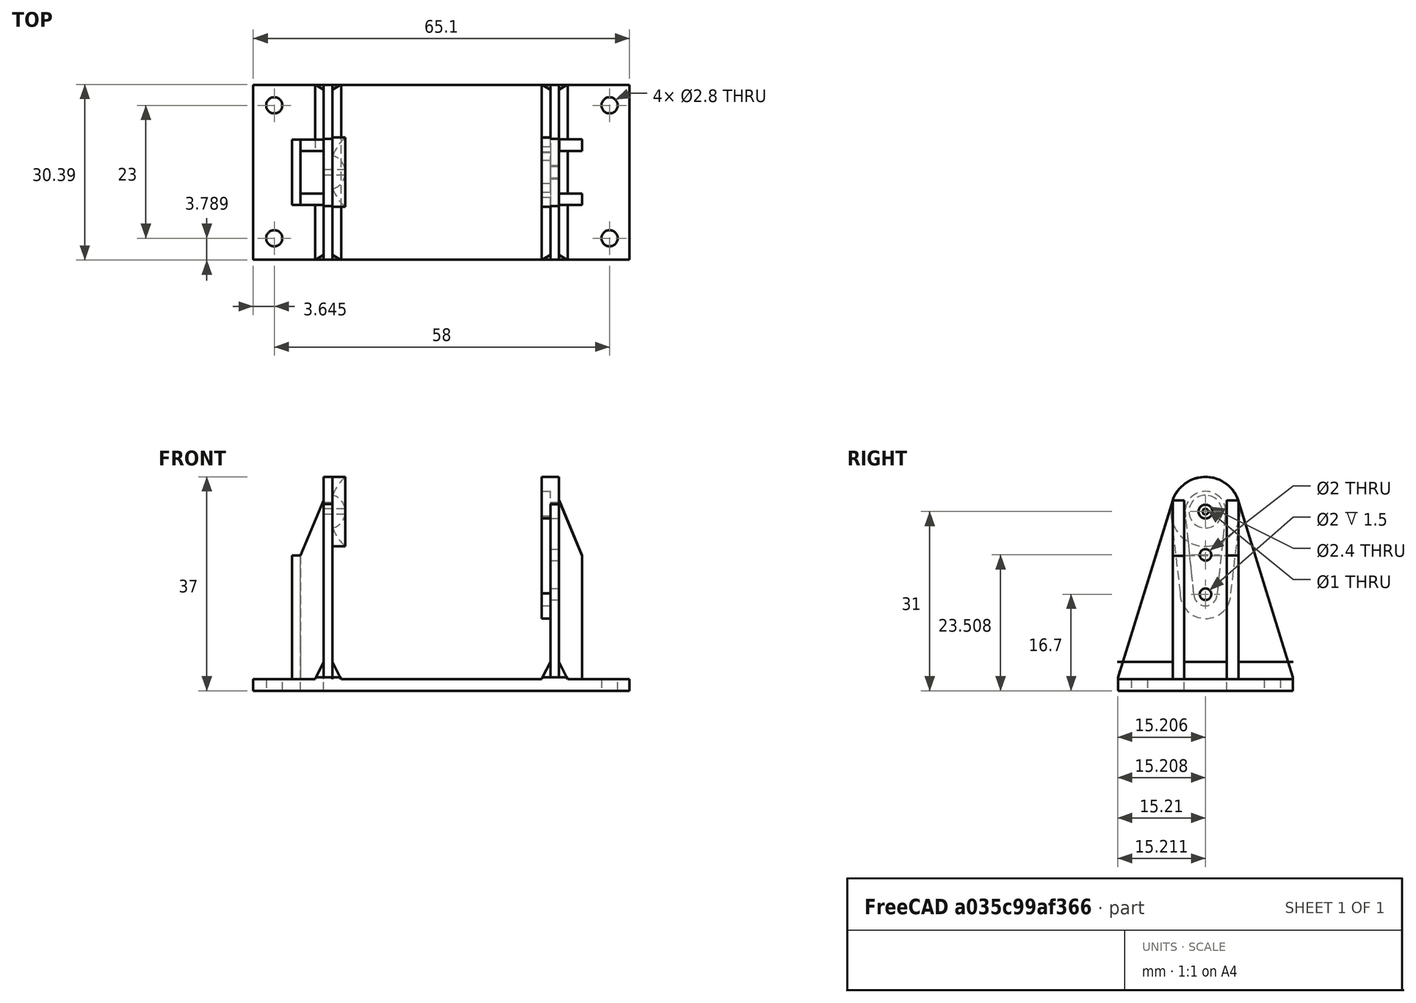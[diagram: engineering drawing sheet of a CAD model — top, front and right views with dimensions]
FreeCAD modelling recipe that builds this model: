
FCSTD DOCUMENT  (FreeCAD 0.18.3R)
Label: Arms
License: All rights reserved
LicenseURL: http://en.wikipedia.org/wiki/All_rights_reserved
objects: Part::Part2DObjectPython×24, Part::Extrusion×17, Part::Cut×11, Part::MultiFuse×6, App::DocumentObjectGroup×2
note: 58 computed .brp shape members not serialized (recipe doc carries the construction recipe); baked Part::Feature solids carry a one-line shape summary decoded from their .brp

FEATURE [Part::Part2DObjectPython] Line006  # Draft 2D object (typed FeaturePython)
  ChamferSize = 0
  Closed = false
  End = (53.5252,-151.594,31)
  FilletRadius = 0
  Length = 2.4
  MakeFace = true
  Placement = pos=(53.5252,-149.194,31) rot=(-1,0,0;1.5708rad)
  Points = (2) [(0,0,0),(0,0,-2.4)]
  Start = (53.5252,-149.194,31)
  Subdivisions = 0
FEATURE [App::DocumentObjectGroup] GrExplode_Slice001  label="Exploded Slice001"
FEATURE [App::DocumentObjectGroup] GrExplode_Slice  label="Exploded Slice"
FEATURE [Part::Part2DObjectPython] Line013  # Draft 2D object (typed FeaturePython)
  ChamferSize = 0
  Closed = false
  End = (34.5802,-150.49,31)
  FilletRadius = 0
  Length = 29
  MakeFace = true
  Placement = pos=(34.5802,-150.506,2) rot=(0.57735,-0.57735,0.57735;4.18879rad)
  Points = (2) [(0,0,0),(-0.0156504,-29,-7.19697e-07)]
  Start = (34.5802,-150.506,2)
  Subdivisions = 0
FEATURE [Part::Part2DObjectPython] Line010  # Draft 2D object (typed FeaturePython)
  ChamferSize = 0
  Closed = false
  End = (15.7302,-144.391,31)
  FilletRadius = 0
  Length = 12.2
  MakeFace = true
  Placement = pos=(15.7302,-156.591,31) rot=(0.57735,-0.57735,0.57735;4.18879rad)
  Points = (2) [(0,0,0),(-12.2,0,0)]
  Start = (15.7302,-156.591,31)
  Subdivisions = 0
FEATURE [Part::Part2DObjectPython] Line  # Draft 2D object (typed FeaturePython)
  ChamferSize = 0
  Closed = false
  End = (53.4302,-150.489,31)
  FilletRadius = 0
  Length = 37.7
  MakeFace = true
  Placement = pos=(15.7302,-150.491,31) rot=(0.57735,0.57735,-0.57735;4.18879rad)
  Points = (2) [(0,0,0),(0.00173367,0,-37.7)]
  Start = (15.7302,-150.491,31)
  Subdivisions = 0
FEATURE [Part::Part2DObjectPython] Line014  # Draft 2D object (typed FeaturePython)
  ChamferSize = 0
  Closed = false
  End = (67.1302,-150.506,-7.22776)
  FilletRadius = 0
  Length = 16.9555
  MakeFace = true
  Placement = pos=(67.1302,-150.506,9.72776) rot=(0.57735,-0.57735,0.57735;4.18879rad)
  Points = (2) [(0,0,0),(0,16.9555,0)]
  Start = (67.1302,-150.506,9.72776)
  Subdivisions = 0
FEATURE [Part::Part2DObjectPython] Rectangle001  # Draft 2D object (typed FeaturePython)
  ChamferSize = 0
  Columns = 1
  FilletRadius = 0
  Height = 30.9198
  Length = 2
  MakeFace = true
  Placement = pos=(55.0252,-156.055,2) rot=(0.57735,0.57735,0.57735;2.0944rad)
  Rows = 1
FEATURE [Part::Part2DObjectPython] Rectangle002  # Draft 2D object (typed FeaturePython)
  ChamferSize = 0
  Columns = 1
  FilletRadius = 0
  Height = 30.9198
  Length = 2
  MakeFace = true
  Placement = pos=(55.0252,-146.712,2) rot=(0.57735,0.57735,0.57735;2.0944rad)
  Rows = 1
FEATURE [Part::Part2DObjectPython] Rectangle003  # Draft 2D object (typed FeaturePython)
  ChamferSize = 0
  Columns = 1
  FilletRadius = 0
  Height = 30.9198
  Length = 2
  MakeFace = true
  Placement = pos=(14.3252,-156.057,2) rot=(0.57735,0.57735,0.57735;2.0944rad)
  Rows = 1
FEATURE [Part::Part2DObjectPython] Rectangle004  # Draft 2D object (typed FeaturePython)
  ChamferSize = 0
  Columns = 1
  FilletRadius = 0
  Height = 30.9198
  Length = 2
  MakeFace = true
  Placement = pos=(14.3252,-146.735,2.06032) rot=(0.57735,0.57735,0.57735;2.0944rad)
  Rows = 1
FEATURE [Part::Extrusion] Extrude
  Base = -> Rectangle003
  Dir = (1,0,0)
  DirMode = 2
  FaceMakerClass = Part::FaceMakerBullseye
  LengthFwd = -4
  LengthRev = 0
  Solid = false
  Symmetric = false
FEATURE [Part::Extrusion] Extrude001
  Base = -> Rectangle004
  Dir = (1,0,0)
  DirMode = 2
  FaceMakerClass = Part::FaceMakerBullseye
  LengthFwd = -4
  LengthRev = 0
  Solid = false
  Symmetric = false
FEATURE [Part::Extrusion] Extrude002
  Base = -> Rectangle001
  Dir = (1,0,0)
  DirMode = 2
  FaceMakerClass = Part::FaceMakerBullseye
  LengthFwd = 4
  LengthRev = 0
  Solid = false
  Symmetric = false
FEATURE [Part::Extrusion] Extrude003
  Base = -> Rectangle002
  Dir = (1,0,0)
  DirMode = 2
  FaceMakerClass = Part::FaceMakerBullseye
  LengthFwd = 4
  LengthRev = 0
  Solid = false
  Symmetric = false
FEATURE [Part::Part2DObjectPython] Wire  # Draft 2D object (typed FeaturePython)
  ChamferSize = 0
  Closed = true
  End = (59.0252,-156.055,32.9198)
  FilletRadius = 0
  Length = 23.9468
  MakeFace = true
  Placement = pos=(55.0252,-156.055,32.9198) rot=(0.57735,-0.57735,-0.57735;2.0944rad)
  Points = (3) [(0,0,0),(-9.03045e-07,-9.57236,-4),(0,0,-4)]
  Start = (55.0252,-156.055,32.9198)
  Subdivisions = 0
FEATURE [Part::MultiFuse] Fusion053
  Placement = pos=(1.1,-300.821,2.5) rot=(1,0,0;3.14159rad)
FEATURE [Part::Extrusion] Extrude005
  Base = -> Wire
  Dir = (0,11.3221,0.0603199)
  DirLink = -> Fusion053 [Edge102]
  DirMode = 1
  FaceMakerClass = Part::FaceMakerBullseye
  LengthFwd = -29
  LengthRev = -19
  Solid = false
  Symmetric = false
FEATURE [Part::MultiFuse] Fusion
  Shapes = -> [Extrude002,Extrude003]
FEATURE [Part::Cut] Cut
  Base = -> Fusion
  Tool = -> Extrude005
FEATURE [Part::Part2DObjectPython] Circle044  # Draft 2D object (typed FeaturePython)
  FirstAngle = 0
  LastAngle = 0
  MakeFace = true
  Placement = pos=(63.6752,-161.911,0.5) rot=(0,0,1;0rad)
  Radius = 1.4
FEATURE [Part::Extrusion] Extrude179
  Base = -> Circle044
  Dir = (0,0,1)
  DirMode = 2
  FaceMakerClass = Part::FaceMakerBullseye
  LengthFwd = 2
  LengthRev = 0
  Placement = pos=(0,0,-0.5) rot=(0,0,1;0rad)
  Solid = false
  Symmetric = false
FEATURE [Part::Part2DObjectPython] Circle043  # Draft 2D object (typed FeaturePython)
  FirstAngle = 0
  LastAngle = 0
  MakeFace = true
  Placement = pos=(63.6752,-138.911,0.5) rot=(0,0,1;0rad)
  Radius = 1.4
FEATURE [Part::Extrusion] Extrude178
  Base = -> Circle043
  Dir = (0,0,1)
  DirMode = 2
  FaceMakerClass = Part::FaceMakerBullseye
  LengthFwd = 2
  LengthRev = 0
  Placement = pos=(0,0,-0.5) rot=(0,0,1;0rad)
  Solid = false
  Symmetric = false
FEATURE [Part::Part2DObjectPython] Circle041  # Draft 2D object (typed FeaturePython)
  FirstAngle = 0
  LastAngle = 0
  MakeFace = true
  Placement = pos=(5.67515,-138.911,0.5) rot=(0,0,1;0rad)
  Radius = 1.4
FEATURE [Part::Extrusion] Extrude176
  Base = -> Circle041
  Dir = (0,0,1)
  DirMode = 2
  FaceMakerClass = Part::FaceMakerBullseye
  LengthFwd = 2
  LengthRev = 0
  Placement = pos=(0,0,-0.5) rot=(0,0,1;0rad)
  Solid = false
  Symmetric = false
FEATURE [Part::Part2DObjectPython] Circle042  # Draft 2D object (typed FeaturePython)
  FirstAngle = 0
  LastAngle = 0
  MakeFace = true
  Placement = pos=(5.67515,-161.911,0.5) rot=(0,0,1;0rad)
  Radius = 1.4
FEATURE [Part::Extrusion] Extrude177
  Base = -> Circle042
  Dir = (0,0,1)
  DirMode = 2
  FaceMakerClass = Part::FaceMakerBullseye
  LengthFwd = 2
  LengthRev = 0
  Placement = pos=(0,0,-0.5) rot=(0,0,1;0rad)
  Solid = false
  Symmetric = false
FEATURE [Part::Part2DObjectPython] Rectangle073  # Draft 2D object (typed FeaturePython)
  ChamferSize = 0
  Columns = 1
  FilletRadius = 0
  Height = 30.2
  Length = 65.1
  MakeFace = true
  Placement = pos=(2.03015,-165.606,0.5) rot=(0,0,1;0rad)
  Rows = 1
FEATURE [Part::Extrusion] Extrude180
  Base = -> Rectangle073
  Dir = (0,0,1)
  DirMode = 2
  FaceMakerClass = Part::FaceMakerBullseye
  LengthFwd = 2
  LengthRev = 0
  Placement = pos=(0,0,-0.5) rot=(0,0,1;0rad)
  Solid = false
  Symmetric = false
FEATURE [Part::Part2DObjectPython] Rectangle  # Draft 2D object (typed FeaturePython)
  ChamferSize = 0
  Columns = 1
  FilletRadius = 0
  Height = 65.1
  Length = 9.62449
  MakeFace = true
  Placement = pos=(2.03015,-135.406,0.5) rot=(0.707107,0.707107,0;3.14159rad)
  Rows = 1
FEATURE [Part::Extrusion] Extrude181
  Base = -> Rectangle
  Dir = (0,0,-1)
  DirMode = 2
  FaceMakerClass = Part::FaceMakerBullseye
  LengthFwd = -4
  LengthRev = 0
  Solid = false
  Symmetric = false
FEATURE [Part::Part2DObjectPython] Rectangle074  # Draft 2D object (typed FeaturePython)
  ChamferSize = 0
  Columns = 1
  FilletRadius = 0
  Height = 65.1
  Length = 7.3643
  MakeFace = true
  Placement = pos=(2.03015,-172.97,0.5) rot=(0.707107,0.707107,0;3.14159rad)
  Rows = 1
FEATURE [Part::Extrusion] Extrude182
  Base = -> Rectangle074
  Dir = (0,0,-1)
  DirMode = 2
  FaceMakerClass = Part::FaceMakerBullseye
  LengthFwd = -4
  LengthRev = 0
  Solid = false
  Symmetric = false
FEATURE [Part::Cut] Cut100
  Base = -> Extrude180
  Tool = -> Extrude176
FEATURE [Part::Cut] Cut101
  Base = -> Cut100
  Tool = -> Extrude177
FEATURE [Part::Cut] Cut102
  Base = -> Cut101
  Tool = -> Extrude178
FEATURE [Part::Cut] Cut103
  Base = -> Cut102
  Tool = -> Extrude179
FEATURE [Part::Part2DObjectPython] Wire001  # Draft 2D object (typed FeaturePython)
  ChamferSize = 0
  Closed = true
  End = (10.3252,-144.735,32.9801)
  FilletRadius = 0
  Length = 23.9688
  MakeFace = true
  Placement = pos=(14.3252,-144.735,32.9801) rot=(-1,0,0;1.5708rad)
  Points = (3) [(0,0,0),(-4,9.58377,-4.92588e-06),(-4,0,0)]
  Start = (14.3252,-144.735,32.9801)
  Subdivisions = 0
FEATURE [Part::Extrusion] Extrude006
  Base = -> Wire001
  Dir = (0,1,2e-16)
  DirMode = 2
  FaceMakerClass = Part::FaceMakerBullseye
  LengthFwd = -30
  LengthRev = 0
  Solid = false
  Symmetric = false
FEATURE [Part::MultiFuse] Fusion054
  Shapes = -> [Extrude001,Extrude]
FEATURE [Part::Cut] Cut096
  Base = -> Fusion054
  Tool = -> Extrude006
FEATURE [Part::Part2DObjectPython] Wire002  # Draft 2D object (typed FeaturePython)
  ChamferSize = 0
  Closed = true
  End = (10.3252,-144.735,32.9801)
  FilletRadius = 0
  Length = 23.9688
  MakeFace = true
  Placement = pos=(14.3252,-144.735,32.9801) rot=(-1,0,0;1.5708rad)
  Points = (3) [(0,0,0),(-4,9.58377,-4.92588e-06),(-4,0,0)]
  Start = (14.3252,-144.735,32.9801)
  Subdivisions = 0
  Support = -> [Cut096]
FEATURE [Part::Extrusion] Extrude007
  Base = -> Wire002
  Dir = (0,1,2e-16)
  DirMode = 2
  FaceMakerClass = Part::FaceMakerBullseye
  LengthFwd = 10
  LengthRev = 0
  Solid = false
  Symmetric = false
FEATURE [Part::Cut] Cut097
  Base = -> Cut096
  Tool = -> Extrude007
FEATURE [Part::MultiFuse] Fusion055
  Placement = pos=(-0.095,-0.095,-4.9e-15) rot=(0,0,1;0rad)
  Shapes = -> [Fusion053,Cut097,Cut]
FEATURE [Part::Cut] Cut098
  Base = -> Fusion055
  Tool = -> Extrude181
FEATURE [Part::Cut] Cut099
  Base = -> Cut098
  Tool = -> Extrude182
FEATURE [Part::Part2DObjectPython] Rectangle076  # Draft 2D object (typed FeaturePython)
  ChamferSize = 0
  Columns = 1
  FilletRadius = 0
  Height = 21.3963
  Length = 11.3283
  MakeFace = true
  Placement = pos=(10.2302,-144.824,2) rot=(0.57735,-0.57735,-0.57735;2.0944rad)
  Rows = 1
  Support = -> [Cut099]
FEATURE [Part::Extrusion] Extrude184
  Base = -> Rectangle076
  Dir = (-1,0,0)
  DirMode = 2
  FaceMakerClass = Part::FaceMakerBullseye
  LengthFwd = 1.5
  LengthRev = 0
  Solid = false
  Symmetric = false
FEATURE [Part::Part2DObjectPython] Line015  # Draft 2D object (typed FeaturePython)
  ChamferSize = 0
  Closed = false
  End = (14.0481,-156.152,23.3963)
  FilletRadius = 0
  Length = 3.81795
  MakeFace = true
  Placement = pos=(10.2302,-156.152,23.3963) rot=(1,0,0;1.5708rad)
  Points = (2) [(0,0,0),(3.81795,0,0)]
  Start = (10.2302,-156.152,23.3963)
  Subdivisions = 0
  Support = -> [Cut099]
FEATURE [Part::Part2DObjectPython] Rectangle077  # Draft 2D object (typed FeaturePython)
  ChamferSize = 0
  Columns = 1
  FilletRadius = 0
  Height = 7.3221
  Length = 4
  MakeFace = true
  Placement = pos=(10.2302,-146.83,-4e-15) rot=(1,0,0;3.14159rad)
  Rows = 1
  Support = -> [Cut103]
FEATURE [Part::Extrusion] Extrude185
  Base = -> Rectangle077
  Dir = (0,0,-1)
  DirMode = 2
  FaceMakerClass = Part::FaceMakerBullseye
  LengthFwd = -2
  LengthRev = 0
  Solid = false
  Symmetric = false
FEATURE [Part::Cut] Cut104
  Base = -> Cut103
  Tool = -> Extrude185
FEATURE [Part::Part2DObjectPython] Rectangle078  # Draft 2D object (typed FeaturePython)
  ChamferSize = 0
  Columns = 1
  FilletRadius = 0
  Height = 7.3221
  Length = 4
  MakeFace = true
  Placement = pos=(10.2302,-146.83,-4e-15) rot=(1,0,0;3.14159rad)
  Rows = 1
  Support = -> [Cut104]
FEATURE [Part::Extrusion] Extrude186
  Base = -> Rectangle078
  Dir = (0,0,-1)
  DirMode = 2
  FaceMakerClass = Part::FaceMakerBullseye
  LengthFwd = -8
  LengthRev = 0
  Solid = false
  Symmetric = false
FEATURE [Part::Cut] Cut105
  Base = -> Cut099
  Tool = -> Extrude186
FEATURE [Part::Part2DObjectPython] Line003  # Draft 2D object (typed FeaturePython)
  ChamferSize = 0
  Closed = false
  End = (2.03015,-150.506,2)
  FilletRadius = 0
  Length = 65.1
  MakeFace = true
  Placement = pos=(67.1302,-150.506,2) rot=(0.57735,-0.57735,0.57735;4.18879rad)
  Points = (2) [(0,0,0),(0,1.10699e-16,-65.1)]
  Start = (67.1302,-150.506,2)
  Subdivisions = 0
FEATURE [Part::MultiFuse] Fusion056
  Shapes = -> [Cut105,Extrude184]
FEATURE [Part::MultiFuse] Fusion057
  Shapes = -> [Cut104,Fusion056]
